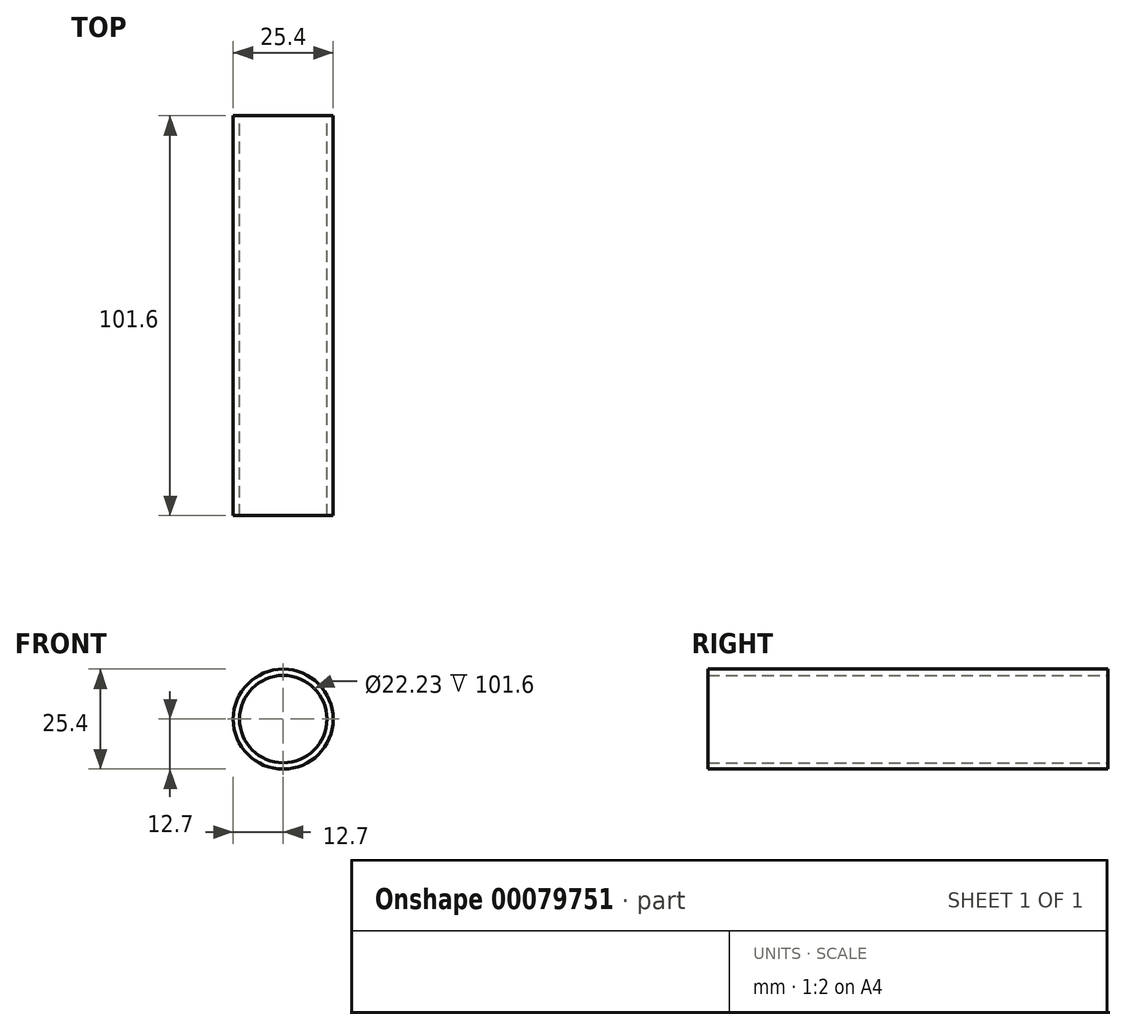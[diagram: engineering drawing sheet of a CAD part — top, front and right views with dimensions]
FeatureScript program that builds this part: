
annotation { "Feature Type Name" : "Feature", "Feature Type Description" : "" }
export const myFeature = defineFeature(function(context is Context, id is Id, definition is map)
    precondition{}
    {
        {
            var Q0;
            Q0=qCreatedBy(makeId("Front.planeOp"),FACE);
            var sketch = newSketch(context, id + "F0", { "sketchPlane" : qUnion([Q0])});
            skCircle(sketch, "E0", {"center": v(0, 0) * mm, "radius": 11.11 * mm});
            skCircle(sketch, "E1", {"center": v(0, 0) * mm, "radius": 12.7 * mm});
            skSolve(sketch);
        }
        {
            var Q0;
            Q0 = qSketchRegion(id + "F0", true);
            extrude(context, id + "F1", {"entities" : qUnion([Q0]), "depth" : 101.6 * mm});
        }
    });
